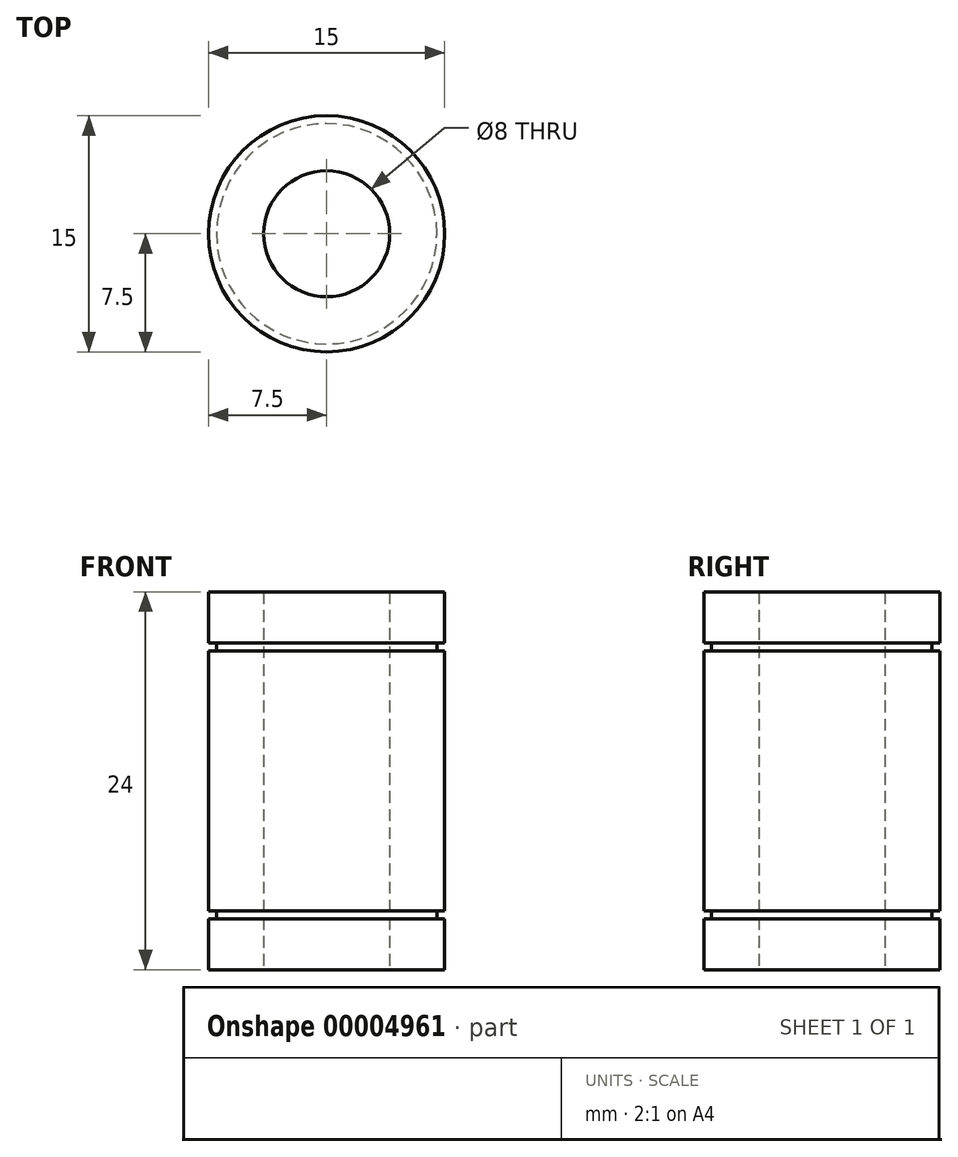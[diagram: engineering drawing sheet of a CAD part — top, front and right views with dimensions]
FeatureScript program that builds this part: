
annotation { "Feature Type Name" : "Feature", "Feature Type Description" : "" }
export const myFeature = defineFeature(function(context is Context, id is Id, definition is map)
    precondition{}
    {
        {
            var Q0;
            Q0=qCreatedBy(makeId("Front.planeOp"),FACE);
            var sketch = newSketch(context, id + "F0", { "sketchPlane" : qUnion([Q0])});
            skLineSegment(sketch, "E0", {"start": v(0, 0) * mm, "end": v(0, 24) * mm, "construction": true});
            skLineSegment(sketch, "E1.bottom", {"start": v(4, 24) * mm, "end": v(7.5, 24) * mm});
            skLineSegment(sketch, "E1.top", {"start": v(4, 0) * mm, "end": v(7.5, 0) * mm});
            skLineSegment(sketch, "E1.left", {"start": v(4, 24) * mm, "end": v(4, 0) * mm});
            skLineSegment(sketch, "E1.right", {"start": v(7.5, 24) * mm, "end": v(7.5, 0) * mm, "construction": true});
            skLineSegment(sketch, "E2", {"start": v(7.5, 24) * mm, "end": v(7.5, 20.75) * mm});
            skLineSegment(sketch, "E3", {"start": v(7.5, 20.75) * mm, "end": v(7, 20.75) * mm});
            skLineSegment(sketch, "E4", {"start": v(7, 20.75) * mm, "end": v(7, 20.25) * mm});
            skLineSegment(sketch, "E5", {"start": v(7, 20.25) * mm, "end": v(7.5, 20.25) * mm});
            skLineSegment(sketch, "E6", {"start": v(7.5, 20.25) * mm, "end": v(7.5, 3.75) * mm});
            skLineSegment(sketch, "E7", {"start": v(7.5, 3.75) * mm, "end": v(7, 3.75) * mm});
            skLineSegment(sketch, "E8", {"start": v(7, 3.75) * mm, "end": v(7, 3.25) * mm});
            skLineSegment(sketch, "E9", {"start": v(7, 3.25) * mm, "end": v(7.5, 3.25) * mm});
            skLineSegment(sketch, "E10", {"start": v(7.5, 3.25) * mm, "end": v(7.5, 0) * mm});
            skSolve(sketch);
        }
        {
            var Q0;
            Q0 = qSketchRegion(id + "F0", true);
            var Q1;
            Q1=sQuery(id+"F0.wireOp",EDGE,"E0");
            revolve(context, id + "F1", {"entities" : qUnion([Q0]), "axis" : qUnion([Q1]), "revolveType" : RevolveType.FULL});
        }
    });
